annotation { "Feature Type Name" : "Feature", "Feature Type Description" : "" }
export const myFeature = defineFeature(function(context is Context, id is Id, definition is map)
    precondition{}
    {
        {
            var Q0;
            Q0=qCreatedBy(makeId("Top.planeOp"),FACE);
            var sketch = newSketch(context, id + "F0", { "sketchPlane" : qUnion([Q0])});
            skLineSegment(sketch, "E0.bottom", {"start": v(-36.25, 22) * mm, "end": v(69.7, 22) * mm});
            skLineSegment(sketch, "E0.top", {"start": v(-36.25, -18) * mm, "end": v(69.7, -18) * mm});
            skLineSegment(sketch, "E0.left", {"start": v(-36.25, 22) * mm, "end": v(-36.25, -18) * mm});
            skLineSegment(sketch, "E0.right", {"start": v(69.7, 22) * mm, "end": v(69.7, -18) * mm});
            skLineSegment(sketch, "E1", {"start": v(-36.25, 22) * mm, "end": v(-53.56, 4.69) * mm});
            skLineSegment(sketch, "E2", {"start": v(-53.12, -4.2) * mm, "end": v(-36.25, -18) * mm});
            skPoint(sketch, "E3.visualSharp", {"position": v(-58.25, 0) * mm});
            skArc(sketch, "E3.filletArc", {"start": v(-53.56, 4.69) * mm, "mid": v(-55.31, 0.15) * mm, "end": v(-53.12, -4.2) * mm});
            skCircle(sketch, "E4", {"center": v(-50.25, 0.45) * mm, "radius": 2.5 * mm});
            skText(sketch, "E5", { "text": "Charlene Putney\n10 The Cottages\nStradbrook Road, Blackrock\nCo. Dublin, IRELAND", "fontName": "AllertaStencil-Regular.ttf"});
            const initialGuessF0  = {"E5": [-0.03125, 0.012, 1, 0, 0.005]};
            skSetInitialGuess(sketch, initialGuessF0);
            skSolve(sketch);
        }
        {
            var Q0;
            Q0=makeQuery(id+"F0.imprint","IMPRINT",FACE,{"disambiguationData":[TD([[makeQuery(id+"F0.imprint","IMPRINT",EDGE,{"derivedFrom":sQuery(id+"F0.wireOp",EDGE,"E0.left")}),-1.0]])]});
            var Q1;
            Q1=makeQuery(id+"F0.imprint","IMPRINT",FACE,{"disambiguationData":[TD([[makeQuery(id+"F0.imprint","IMPRINT",EDGE,{"derivedFrom":sQuery(id+"F0.wireOp",EDGE,"E0.bottom")}),-1.0]])]});
            extrude(context, id + "F1", {"entities" : qUnion([Q0, Q1]), "depth" : 2.4 * mm, "offsetDistance" : 25 * mm});
        }
    });